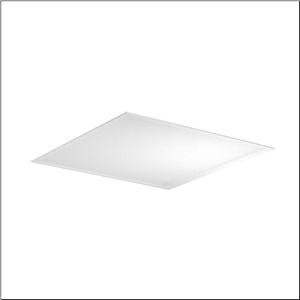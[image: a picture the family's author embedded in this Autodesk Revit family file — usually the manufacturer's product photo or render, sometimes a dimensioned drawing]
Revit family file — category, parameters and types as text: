
# Revit family: apollon_r__31_square_51mp12wd2442_6000
name_source: partatom
category: Lighting Fixtures
units: mm (PartAtom-declared; Revit-internal decimal feet)

## family parameters
Cut with Voids When Loaded = No
Host = Face
Light Source = No
Part Type = Normal
Room Calculation Point = No
Round Connector Dimension = Use Diameter
Shared = No

## types (1)
- Apollon® 31 square (1 x LED, 3800 lm, 27.5 W, 4000K)
    Apparent Load = 28 VA
    CIE Flux Codes = 61 87 97 100 100
    Color Rendering = 80
    Color Temperature = 4000K
    Default Elevation = 1800 mm
    Description = Apollon® 31 square, office luminaire, primary optical cover: micro prismatic cover, of PMMA, CAT 2 (L<= 3000cd/m²), light emission: direct distribution, primary light characteristic: symmetric, installation type: lay-in mounting, LED, rated luminous flux: 3.800lm, luminous efficacy: 138lm/W, light colour: 840, colour temperature: 4000K, with terminal, 5-pole, mains connection: 220..240V, AC/DC, 0/50..60Hz, rated input power: 28W, housing, of aluminium, traffic white (RAL 9016), module: M600, length: 595mm, width: 595mm, height: 32mm, housing upper side, of sheet steel, galvanised, protection rating (complete): IP20, protection rating (on room side): IP40, insulation class (complete): insulation class II (safety insulation), certification: CE, ENEC, impact resistance: IK03, permissible operating ambient temperature: -20..+40°C, permissible storage temperature: -20..+60°C, packaging unit: 1 piece
    Height = 0 mm  [stored 0 ft]
    Lamp = 1 x LED
    Lamp Light Flux = 3800 lm
    Lamp Power = 27.5 W
    Lamp count = 1
    Length = 595 mm
    Luminous efficacy = 138 lm/W
    Manufacturer = Siteco
    ModVariant = No
    Model = 51MP12WD2442
    Mounting Place = Ceiling
    Mounting Type = Recessed
    Number of Poles = 1
    OnlyDefault = Yes
    Power Factor = 1
    Product Name = Apollon® 31 square
    Product group = office luminaire | ceiling recessed
    ProductGroupID = 401
    Protection Class = Protection class II
    Protection Degree = IP 20
    RLX_Detail_Level = 1
    RLX_Emergency_Light_Flux = 0 lm
    RLX_Emergency_Type = 0
    RLX_Emergency_Type_DB = No
    RlxData = <blob elided: 12473 chars, md5=687048fc>
    Socket = socket
    Standby Power = 0 W
    System Light Flux = 3800 lm
    System Power = 28 W
    Type Comments = Product without accessories
    Type Image = l_1291035.jpg
    URL = http://relux.com
    VarID = ---
    Voltage = 0 V
    Weight = 0.00 kg
    Width = 595 mm

note: [stored X ft] marks values corroborated as IEEE doubles in the binary element streams (Revit-internal decimal feet)

## geometry (parser evidence)
native form markers: Sweep x11
no freeform markers — native parametric forms only
